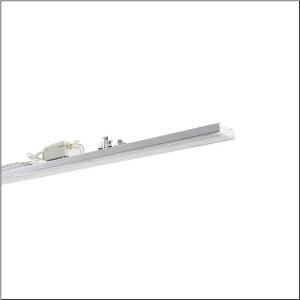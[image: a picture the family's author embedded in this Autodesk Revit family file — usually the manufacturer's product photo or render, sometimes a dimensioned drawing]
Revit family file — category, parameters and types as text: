
# Revit family: licross_11_recessed_mo_51te18dv4e5g
name_source: partatom
category: Lighting Fixtures
units: mm (PartAtom-declared; Revit-internal decimal feet)

## family parameters
Cut with Voids When Loaded = No
Host = Face
Light Source = No
Part Type = Normal
Room Calculation Point = No
Round Connector Dimension = Use Diameter
Shared = No

## types (1)
- --- (1 x LED, 14920 lm, 84.1 W, 4000K)
    Apparent Load = 84 VA
    CIE Flux Codes = 83 96 99 100 100
    Color Rendering = 80
    Color Temperature = 4000K
    Default Elevation = 1800 mm
    Description = Licross 11 Recessed MO, luminaire insert, of sheet steel, galvanised, coil coated, white, length: 2.250mm, width: 66mm, height: 67mm, LED rated luminous flux: 14.920lm, light colour: 840, SDCM (Standard Deviation of Colour Matching)MacAdam ≤ 2 SDCM (initial), control gear: DALI 2, with plug, 5-pole, with phase selection, mains connection: 220..240V, AC, 50/60Hz, rated input power: 84W, internal wiring halogen-free, primary light control with lens, of plastic, primary optical cover: cover, of PMMA, light emission: direct distribution, primary light characteristic: symmetric, protection rating (complete): IP54, insulation class (complete): insulation class I (protective earthing), certification: CE, ENEC, VDE, UKCA, protection symbol: D if used in an environment with non-conductive dust loads with corresponding accessories, impact resistance: IK06, permissible ambient temperature for indoor applications: -25..+35°C, corresponds to IFS (International Featured Standards) requirements for safety and quality in the food industry, reducing of maximum allowable ambient temperature of 5°C with ceiling mounting, LABS conformity tested according to VDMA 24364:2018-05, The light source and the operating device comply with the requirements of the Ecodesign Regulation (EU) 2019/2020 and are replaceable in accordance with this regulation, packaging unit: 1 piece
    Height = 58 mm
    Lamp = 1 x LED
    Lamp Light Flux = 14920 lm
    Lamp Power = 84.1 W
    Lamp count = 1
    Length = 2250 mm
    Luminous efficacy = 177 lm/W
    Manufacturer = Siteco
    ModVariant = No
    Model = 51TE18DV4E5G
    Mounting Place = Ceiling
    Mounting Type = Pendant
    Number of Poles = 1
    OnlyDefault = Yes
    Power Factor = 1
    Product Name = Licross 11 Recessed MO
    Product group = luminaire insert | ceiling pendant
    ProductGroupID = 901
    Protection Class = Protection class I
    Protection Degree = IP 54
    RLX_Detail_Level = 1
    RLX_Emergency_Light_Flux = 0 lm
    RLX_Emergency_Type = 0
    RLX_Emergency_Type_DB = No
    RlxData = <blob elided: 29473 chars, md5=c6f45782>
    Socket = socket
    Standby Power = 0 W
    System Light Flux = 14920 lm
    System Power = 84 W
    Type Comments = factory setting: luminous flux: 100 % | dim-lin: 254 | 378 mA
    Type Image = l_1296930.jpg
    URL = http://relux.com
    VarID = @adj_102125
    Voltage = 0 V
    Weight = 0.00 kg
    Width = 66 mm

## geometry (parser evidence)
native form markers: Blend x4, Sweep x10
no freeform markers — native parametric forms only
